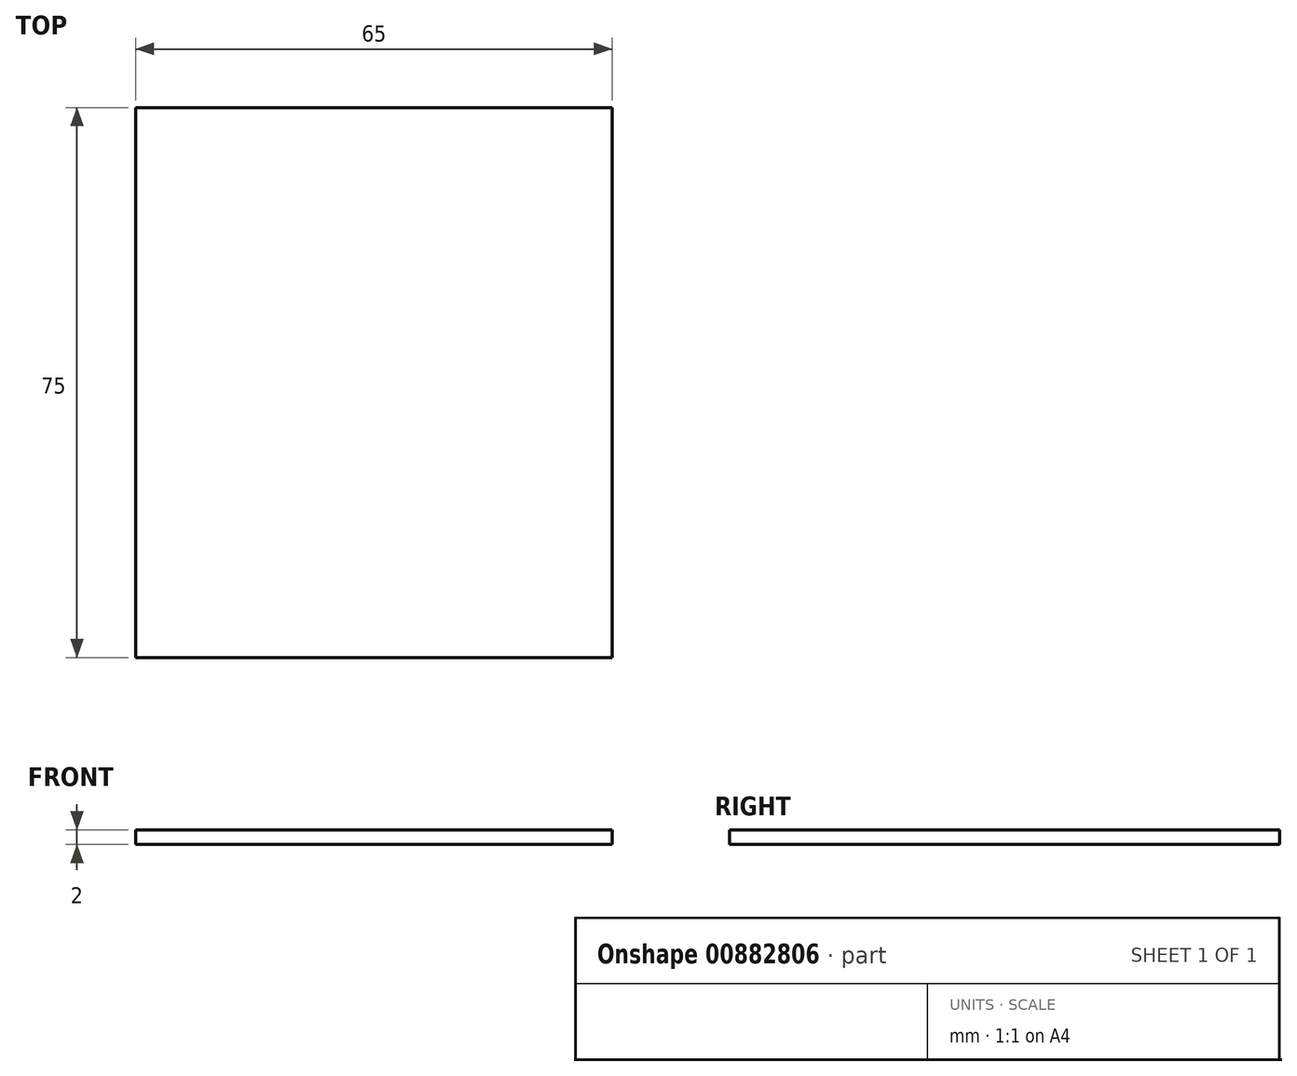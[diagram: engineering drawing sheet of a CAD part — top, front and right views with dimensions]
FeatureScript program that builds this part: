
annotation { "Feature Type Name" : "Feature", "Feature Type Description" : "" }
export const myFeature = defineFeature(function(context is Context, id is Id, definition is map)
    precondition{}
    {
        {
            var Q0;
            Q0=qCreatedBy(makeId("Top.planeOp"),FACE);
            var sketch = newSketch(context, id + "F0", { "sketchPlane" : qUnion([Q0])});
            skLineSegment(sketch, "E0.bottom", {"start": v(0, 0) * mm, "end": v(65, 0) * mm});
            skLineSegment(sketch, "E0.top", {"start": v(0, 75) * mm, "end": v(65, 75) * mm});
            skLineSegment(sketch, "E0.left", {"start": v(0, 0) * mm, "end": v(0, 75) * mm});
            skLineSegment(sketch, "E0.right", {"start": v(65, 0) * mm, "end": v(65, 75) * mm});
            skSolve(sketch);
        }
        {
            var Q0;
            Q0 = qSketchRegion(id + "F0", true);
            extrude(context, id + "F1", {"entities" : qUnion([Q0]), "depth" : 2 * mm, "offsetDistance" : 25 * mm});
        }
    });
